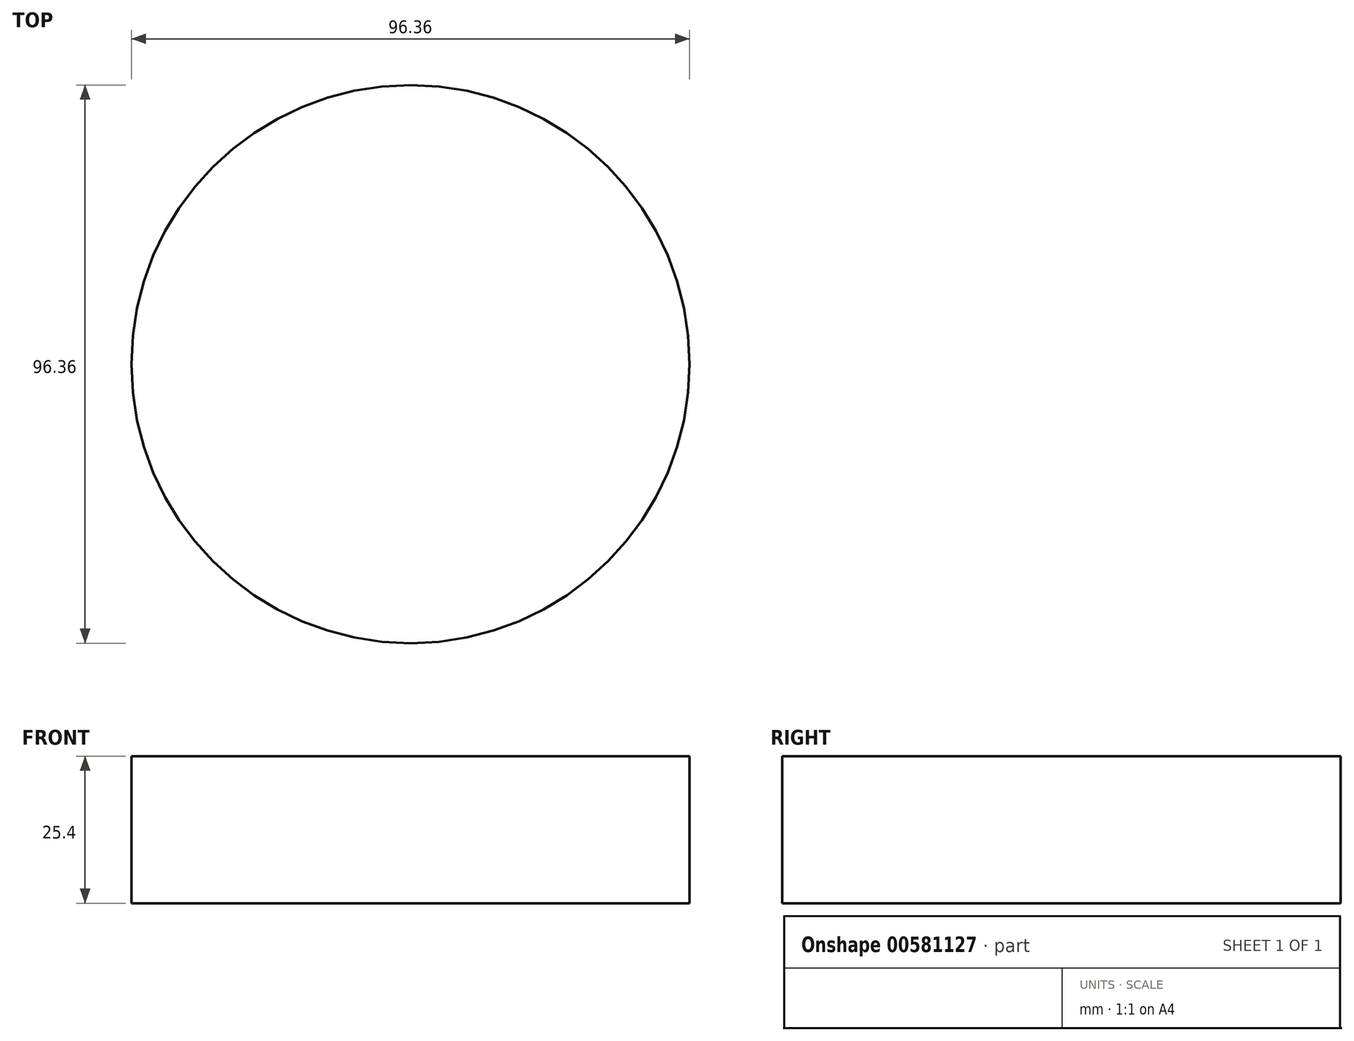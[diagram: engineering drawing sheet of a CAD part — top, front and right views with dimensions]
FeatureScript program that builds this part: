
annotation { "Feature Type Name" : "Feature", "Feature Type Description" : "" }
export const myFeature = defineFeature(function(context is Context, id is Id, definition is map)
    precondition{}
    {
        {
            var Q0;
            Q0=qCreatedBy(makeId("Top.planeOp"),FACE);
            var sketch = newSketch(context, id + "F0", { "sketchPlane" : qUnion([Q0])});
            skCircle(sketch, "E0", {"center": v(-182, -92.04) * mm, "radius": 48.18 * mm});
            skPoint(sketch, "E0.first.point", {"position": v(-181.57, -140.22) * mm});
            skPoint(sketch, "E0.second.point", {"position": v(-133.83, -90.7) * mm});
            skPoint(sketch, "E0.third.point", {"position": v(-218.32, -60.4) * mm});
            skSolve(sketch);
        }
        {
            var Q0;
            Q0 = qSketchRegion(id + "F0", true);
            extrude(context, id + "F1", {"entities" : qUnion([Q0]), "depth" : 25.4 * mm, "offsetDistance" : 25.4 * mm});
        }
    });
